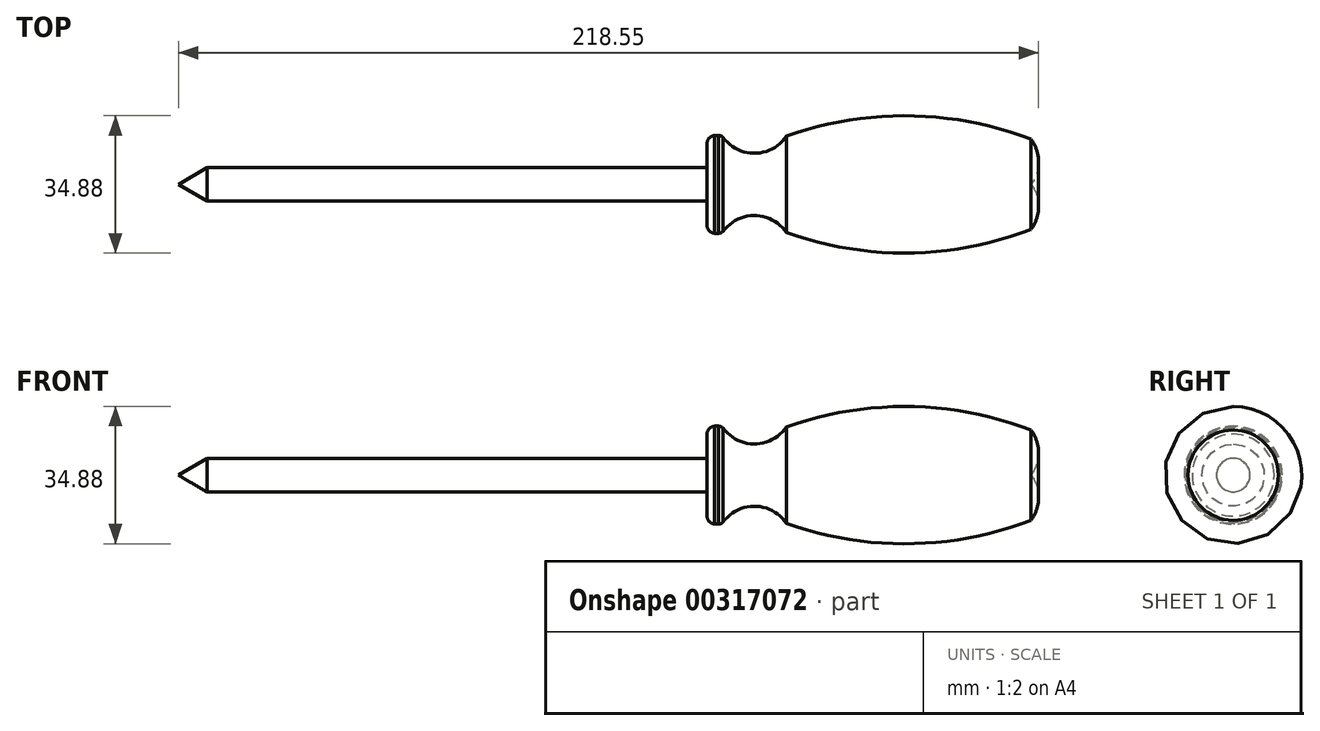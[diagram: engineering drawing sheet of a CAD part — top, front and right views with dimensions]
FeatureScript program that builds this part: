
annotation { "Feature Type Name" : "Feature", "Feature Type Description" : "" }
export const myFeature = defineFeature(function(context is Context, id is Id, definition is map)
    precondition{}
    {
        {
            var Q0;
            Q0=qCreatedBy(makeId("Front.planeOp"),FACE);
            var sketch = newSketch(context, id + "F0", { "sketchPlane" : qUnion([Q0])});
            skLineSegment(sketch, "E0", {"start": v(-140.08, 0) * mm, "end": v(76.65, 0) * mm});
            skLineSegment(sketch, "E1", {"start": v(-140.08, 0) * mm, "end": v(-132.81, 4.27) * mm});
            skLineSegment(sketch, "E2", {"start": v(-132.81, 4.27) * mm, "end": v(-5.81, 4.27) * mm});
            skLineSegment(sketch, "E3", {"start": v(-5.81, 4.27) * mm, "end": v(-5.81, 10.42) * mm});
            skLineSegment(sketch, "E4", {"start": v(-3.9, 12.44) * mm, "end": v(-2.85, 12.44) * mm});
            skLineSegment(sketch, "E5", {"start": v(14.53, 12.44) * mm, "end": v(14.93, 12.44) * mm});
            skLineSegment(sketch, "E6", {"start": v(76.65, 11.41) * mm, "end": v(76.65, 11.3) * mm});
            skArc(sketch, "E7", {"start": v(-1.66, 11.95) * mm, "mid": v(6.56, 7.9) * mm, "end": v(14.53, 12.44) * mm});
            skPoint(sketch, "E7.first.point", {"position": v(0, 10.17) * mm});
            skPoint(sketch, "E7.second.point", {"position": v(6.27, 7.9) * mm});
            skPoint(sketch, "E7.third.point", {"position": v(12.53, 10.17) * mm});
            skPoint(sketch, "E8.orphan", {"position": v(0, 12.44) * mm});
            skPoint(sketch, "E9.end.orphan", {"position": v(0, 7.9) * mm});
            skPoint(sketch, "E10.orphan", {"position": v(12.53, 7.9) * mm});
            skPoint(sketch, "E11.end.orphan", {"position": v(12.53, 12.44) * mm});
            skArc(sketch, "E12", {"start": v(-3.34, 12.44) * mm, "mid": v(-5.13, 11.86) * mm, "end": v(-5.81, 10.12) * mm});
            skPoint(sketch, "E12.first.point", {"position": v(-5.81, 10.42) * mm});
            skPoint(sketch, "E12.second.point", {"position": v(-3.9, 12.44) * mm});
            skPoint(sketch, "E12.third.point", {"position": v(-1.91, 8.9) * mm});
            skPoint(sketch, "E13.orphan", {"position": v(-5.81, 12.44) * mm});
            skArc(sketch, "E14", {"start": v(-1.31, 11.5) * mm, "mid": v(-2, 12.2) * mm, "end": v(-2.95, 12.44) * mm});
            skPoint(sketch, "E14.first.point", {"position": v(-2.95, 12.44) * mm});
            skPoint(sketch, "E14.second.point", {"position": v(-1.31, 11.5) * mm});
            skPoint(sketch, "E14.third.point", {"position": v(-2.95, 8.83) * mm});
            skPoint(sketch, "E14.third.point.positionSnap0", {"position": v(-2.95, 12.44) * mm});
            skPoint(sketch, "E15.orphan", {"position": v(-2, 12.44) * mm});
            skArc(sketch, "E16", {"start": v(76.65, 11.41) * mm, "mid": v(45.6, 17.43) * mm, "end": v(14.4, 12.26) * mm});
            skLineSegment(sketch, "E17.trimOffspring", {"start": v(76.65, 0) * mm, "end": v(76.65, 0) * mm});
            skArc(sketch, "E18.trimOffspring", {"start": v(76.64, 0) * mm, "mid": v(78.47, 5.74) * mm, "end": v(76.55, 11.45) * mm});
            skSolve(sketch);
        }
        {
            var Q0;
            {var subQ15=sQuery(id+"F0.wireOp",EDGE,"E1");Q0=makeQuery(id+"F0.imprint","IMPRINT",FACE,{"disambiguationData":[TD([[makeQuery(id+"F0.imprint","IMPRINT",EDGE,{"derivedFrom":subQ15}),-1.0]])]});}
            var Q1;
            Q1=sQuery(id+"F0.wireOp",EDGE,"E0");
            revolve(context, id + "F1", {"entities" : qUnion([Q0]), "axis" : qUnion([Q1]), "revolveType" : RevolveType.FULL});
        }
    });
